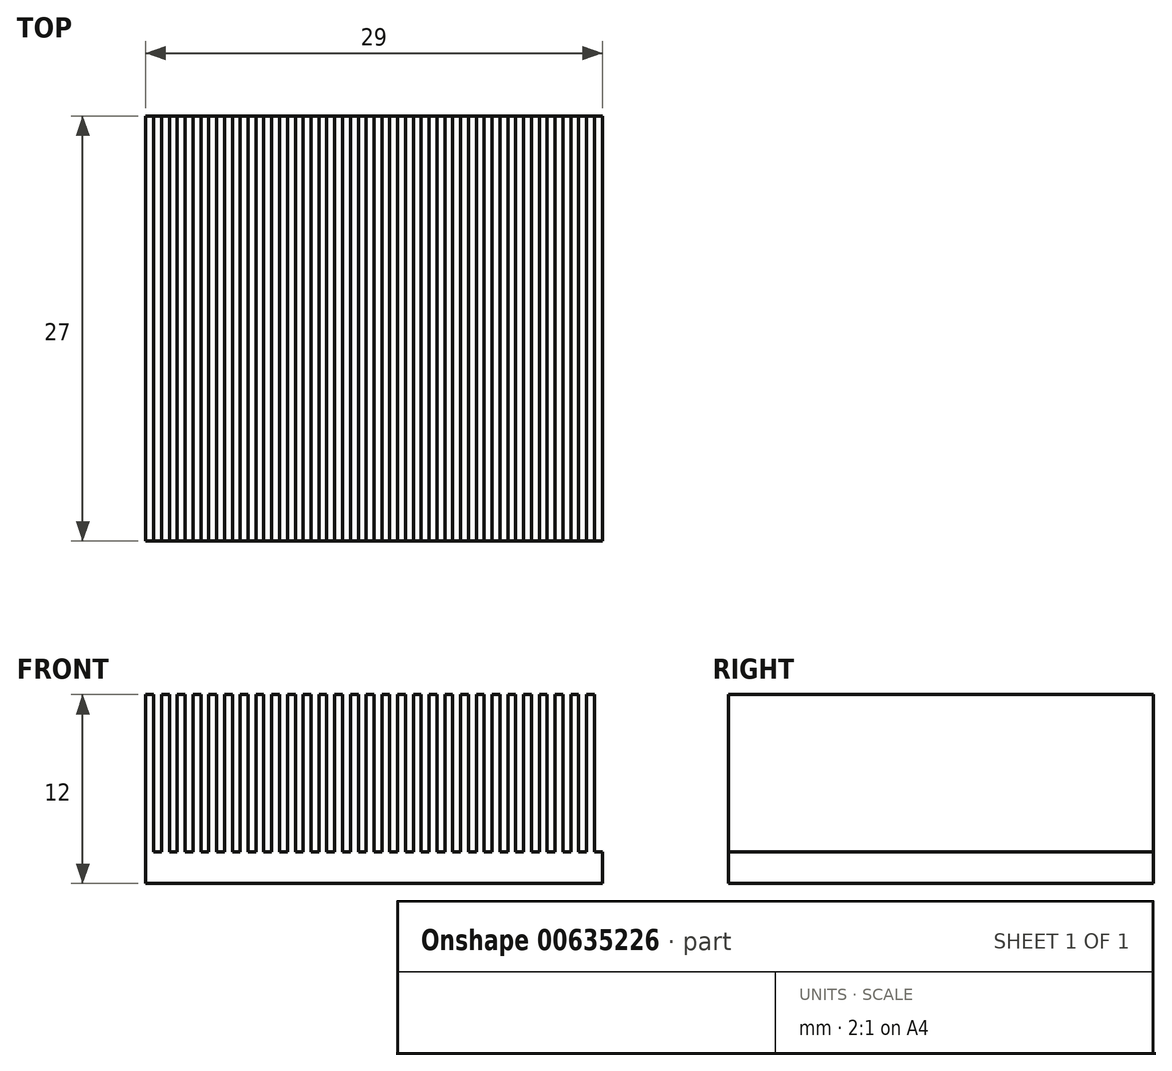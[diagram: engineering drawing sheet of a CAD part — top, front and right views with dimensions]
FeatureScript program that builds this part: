
annotation { "Feature Type Name" : "Feature", "Feature Type Description" : "" }
export const myFeature = defineFeature(function(context is Context, id is Id, definition is map)
    precondition{}
    {
        {
            var Q0;
            Q0=qCreatedBy(makeId("Top.planeOp"),FACE);
            var sketch = newSketch(context, id + "F0", { "sketchPlane" : qUnion([Q0])});
            skLineSegment(sketch, "E0.bottom", {"start": v(14.5, 13.5) * mm, "end": v(-14.5, 13.5) * mm});
            skLineSegment(sketch, "E0.top", {"start": v(14.5, -13.5) * mm, "end": v(-14.5, -13.5) * mm});
            skLineSegment(sketch, "E0.left", {"start": v(14.5, 13.5) * mm, "end": v(14.5, -13.5) * mm});
            skLineSegment(sketch, "E0.right", {"start": v(-14.5, 13.5) * mm, "end": v(-14.5, -13.5) * mm});
            skPoint(sketch, "E0.middle", {"position": v(0, 0) * mm});
            skSolve(sketch);
        }
        {
            var Q0;
            Q0 = qSketchRegion(id + "F0", true);
            extrude(context, id + "F1", {"entities" : qUnion([Q0]), "depth" : 2 * mm, "offsetDistance" : 25 * mm});
        }
        {
            var Q0;
            Q0=makeQuery(id+"F1.opExtrude","CAP_FACE",FACE,{"disambiguationData":[OSD([sQuery(id+"F0.wireOp",EDGE,"E0.bottom"),sQuery(id+"F0.wireOp",EDGE,"E0.top"),sQuery(id+"F0.wireOp",EDGE,"E0.left"),sQuery(id+"F0.wireOp",EDGE,"E0.right")])],"isStart":false});
            var sketch = newSketch(context, id + "F2", { "sketchPlane" : qUnion([Q0])});
            skLineSegment(sketch, "E1.bottom", {"start": v(-14.5, 13.5) * mm, "end": v(-14, 13.5) * mm});
            skLineSegment(sketch, "E1.top", {"start": v(-14.5, -13.5) * mm, "end": v(-14, -13.5) * mm});
            skLineSegment(sketch, "E1.left", {"start": v(-14.5, 13.5) * mm, "end": v(-14.5, -13.5) * mm});
            skLineSegment(sketch, "E1.right", {"start": v(-14, 13.5) * mm, "end": v(-14, -13.5) * mm});
            skLineSegment(sketch, "E2.1.0.0", {"start": v(-13.5, 13.5) * mm, "end": v(-13, 13.5) * mm});
            skLineSegment(sketch, "E2.1.0.1", {"start": v(-13.5, 13.5) * mm, "end": v(-13.5, -13.5) * mm});
            skLineSegment(sketch, "E2.1.0.2", {"start": v(-13, 13.5) * mm, "end": v(-13, -13.5) * mm});
            skLineSegment(sketch, "E2.1.0.3", {"start": v(-13.5, -13.5) * mm, "end": v(-13, -13.5) * mm});
            skLineSegment(sketch, "E2.2.0.0", {"start": v(-12.5, 13.5) * mm, "end": v(-12, 13.5) * mm});
            skLineSegment(sketch, "E2.2.0.1", {"start": v(-12.5, 13.5) * mm, "end": v(-12.5, -13.5) * mm});
            skLineSegment(sketch, "E2.2.0.2", {"start": v(-12, 13.5) * mm, "end": v(-12, -13.5) * mm});
            skLineSegment(sketch, "E2.2.0.3", {"start": v(-12.5, -13.5) * mm, "end": v(-12, -13.5) * mm});
            skLineSegment(sketch, "E2.3.0.0", {"start": v(-11.5, 13.5) * mm, "end": v(-11, 13.5) * mm});
            skLineSegment(sketch, "E2.3.0.1", {"start": v(-11.5, 13.5) * mm, "end": v(-11.5, -13.5) * mm});
            skLineSegment(sketch, "E2.3.0.2", {"start": v(-11, 13.5) * mm, "end": v(-11, -13.5) * mm});
            skLineSegment(sketch, "E2.3.0.3", {"start": v(-11.5, -13.5) * mm, "end": v(-11, -13.5) * mm});
            skLineSegment(sketch, "E2.4.0.0", {"start": v(-10.5, 13.5) * mm, "end": v(-10, 13.5) * mm});
            skLineSegment(sketch, "E2.4.0.1", {"start": v(-10.5, 13.5) * mm, "end": v(-10.5, -13.5) * mm});
            skLineSegment(sketch, "E2.4.0.2", {"start": v(-10, 13.5) * mm, "end": v(-10, -13.5) * mm});
            skLineSegment(sketch, "E2.4.0.3", {"start": v(-10.5, -13.5) * mm, "end": v(-10, -13.5) * mm});
            skLineSegment(sketch, "E2.5.0.0", {"start": v(-9.5, 13.5) * mm, "end": v(-9, 13.5) * mm});
            skLineSegment(sketch, "E2.5.0.1", {"start": v(-9.5, 13.5) * mm, "end": v(-9.5, -13.5) * mm});
            skLineSegment(sketch, "E2.5.0.2", {"start": v(-9, 13.5) * mm, "end": v(-9, -13.5) * mm});
            skLineSegment(sketch, "E2.5.0.3", {"start": v(-9.5, -13.5) * mm, "end": v(-9, -13.5) * mm});
            skLineSegment(sketch, "E2.6.0.0", {"start": v(-8.5, 13.5) * mm, "end": v(-8, 13.5) * mm});
            skLineSegment(sketch, "E2.6.0.1", {"start": v(-8.5, 13.5) * mm, "end": v(-8.5, -13.5) * mm});
            skLineSegment(sketch, "E2.6.0.2", {"start": v(-8, 13.5) * mm, "end": v(-8, -13.5) * mm});
            skLineSegment(sketch, "E2.6.0.3", {"start": v(-8.5, -13.5) * mm, "end": v(-8, -13.5) * mm});
            skLineSegment(sketch, "E2.7.0.0", {"start": v(-7.5, 13.5) * mm, "end": v(-7, 13.5) * mm});
            skLineSegment(sketch, "E2.7.0.1", {"start": v(-7.5, 13.5) * mm, "end": v(-7.5, -13.5) * mm});
            skLineSegment(sketch, "E2.7.0.2", {"start": v(-7, 13.5) * mm, "end": v(-7, -13.5) * mm});
            skLineSegment(sketch, "E2.7.0.3", {"start": v(-7.5, -13.5) * mm, "end": v(-7, -13.5) * mm});
            skLineSegment(sketch, "E2.8.0.0", {"start": v(-6.5, 13.5) * mm, "end": v(-6, 13.5) * mm});
            skLineSegment(sketch, "E2.8.0.1", {"start": v(-6.5, 13.5) * mm, "end": v(-6.5, -13.5) * mm});
            skLineSegment(sketch, "E2.8.0.2", {"start": v(-6, 13.5) * mm, "end": v(-6, -13.5) * mm});
            skLineSegment(sketch, "E2.8.0.3", {"start": v(-6.5, -13.5) * mm, "end": v(-6, -13.5) * mm});
            skLineSegment(sketch, "E2.9.0.0", {"start": v(-5.5, 13.5) * mm, "end": v(-5, 13.5) * mm});
            skLineSegment(sketch, "E2.9.0.1", {"start": v(-5.5, 13.5) * mm, "end": v(-5.5, -13.5) * mm});
            skLineSegment(sketch, "E2.9.0.2", {"start": v(-5, 13.5) * mm, "end": v(-5, -13.5) * mm});
            skLineSegment(sketch, "E2.9.0.3", {"start": v(-5.5, -13.5) * mm, "end": v(-5, -13.5) * mm});
            skLineSegment(sketch, "E2.10.0.0", {"start": v(-4.5, 13.5) * mm, "end": v(-4, 13.5) * mm});
            skLineSegment(sketch, "E2.10.0.1", {"start": v(-4.5, 13.5) * mm, "end": v(-4.5, -13.5) * mm});
            skLineSegment(sketch, "E2.10.0.2", {"start": v(-4, 13.5) * mm, "end": v(-4, -13.5) * mm});
            skLineSegment(sketch, "E2.10.0.3", {"start": v(-4.5, -13.5) * mm, "end": v(-4, -13.5) * mm});
            skLineSegment(sketch, "E2.11.0.0", {"start": v(-3.5, 13.5) * mm, "end": v(-3, 13.5) * mm});
            skLineSegment(sketch, "E2.11.0.1", {"start": v(-3.5, 13.5) * mm, "end": v(-3.5, -13.5) * mm});
            skLineSegment(sketch, "E2.11.0.2", {"start": v(-3, 13.5) * mm, "end": v(-3, -13.5) * mm});
            skLineSegment(sketch, "E2.11.0.3", {"start": v(-3.5, -13.5) * mm, "end": v(-3, -13.5) * mm});
            skLineSegment(sketch, "E2.12.0.0", {"start": v(-2.5, 13.5) * mm, "end": v(-2, 13.5) * mm});
            skLineSegment(sketch, "E2.12.0.1", {"start": v(-2.5, 13.5) * mm, "end": v(-2.5, -13.5) * mm});
            skLineSegment(sketch, "E2.12.0.2", {"start": v(-2, 13.5) * mm, "end": v(-2, -13.5) * mm});
            skLineSegment(sketch, "E2.12.0.3", {"start": v(-2.5, -13.5) * mm, "end": v(-2, -13.5) * mm});
            skLineSegment(sketch, "E2.13.0.0", {"start": v(-1.5, 13.5) * mm, "end": v(-1, 13.5) * mm});
            skLineSegment(sketch, "E2.13.0.1", {"start": v(-1.5, 13.5) * mm, "end": v(-1.5, -13.5) * mm});
            skLineSegment(sketch, "E2.13.0.2", {"start": v(-1, 13.5) * mm, "end": v(-1, -13.5) * mm});
            skLineSegment(sketch, "E2.13.0.3", {"start": v(-1.5, -13.5) * mm, "end": v(-1, -13.5) * mm});
            skLineSegment(sketch, "E2.14.0.0", {"start": v(-0.5, 13.5) * mm, "end": v(0, 13.5) * mm});
            skLineSegment(sketch, "E2.14.0.1", {"start": v(-0.5, 13.5) * mm, "end": v(-0.5, -13.5) * mm});
            skLineSegment(sketch, "E2.14.0.2", {"start": v(0, 13.5) * mm, "end": v(0, -13.5) * mm});
            skLineSegment(sketch, "E2.14.0.3", {"start": v(-0.5, -13.5) * mm, "end": v(0, -13.5) * mm});
            skLineSegment(sketch, "E2.15.0.0", {"start": v(0.5, 13.5) * mm, "end": v(1, 13.5) * mm});
            skLineSegment(sketch, "E2.15.0.1", {"start": v(0.5, 13.5) * mm, "end": v(0.5, -13.5) * mm});
            skLineSegment(sketch, "E2.15.0.2", {"start": v(1, 13.5) * mm, "end": v(1, -13.5) * mm});
            skLineSegment(sketch, "E2.15.0.3", {"start": v(0.5, -13.5) * mm, "end": v(1, -13.5) * mm});
            skLineSegment(sketch, "E2.16.0.0", {"start": v(1.5, 13.5) * mm, "end": v(2, 13.5) * mm});
            skLineSegment(sketch, "E2.16.0.1", {"start": v(1.5, 13.5) * mm, "end": v(1.5, -13.5) * mm});
            skLineSegment(sketch, "E2.16.0.2", {"start": v(2, 13.5) * mm, "end": v(2, -13.5) * mm});
            skLineSegment(sketch, "E2.16.0.3", {"start": v(1.5, -13.5) * mm, "end": v(2, -13.5) * mm});
            skLineSegment(sketch, "E2.17.0.0", {"start": v(2.5, 13.5) * mm, "end": v(3, 13.5) * mm});
            skLineSegment(sketch, "E2.17.0.1", {"start": v(2.5, 13.5) * mm, "end": v(2.5, -13.5) * mm});
            skLineSegment(sketch, "E2.17.0.2", {"start": v(3, 13.5) * mm, "end": v(3, -13.5) * mm});
            skLineSegment(sketch, "E2.17.0.3", {"start": v(2.5, -13.5) * mm, "end": v(3, -13.5) * mm});
            skLineSegment(sketch, "E2.18.0.0", {"start": v(3.5, 13.5) * mm, "end": v(4, 13.5) * mm});
            skLineSegment(sketch, "E2.18.0.1", {"start": v(3.5, 13.5) * mm, "end": v(3.5, -13.5) * mm});
            skLineSegment(sketch, "E2.18.0.2", {"start": v(4, 13.5) * mm, "end": v(4, -13.5) * mm});
            skLineSegment(sketch, "E2.18.0.3", {"start": v(3.5, -13.5) * mm, "end": v(4, -13.5) * mm});
            skLineSegment(sketch, "E2.direction1", {"start": v(-14.5, 13.5) * mm, "end": v(-13.5, 13.5) * mm, "construction": true});
            skLineSegment(sketch, "E3.0.19.0", {"start": v(4.5, 13.5) * mm, "end": v(5, 13.5) * mm});
            skLineSegment(sketch, "E3.3.19.0", {"start": v(4.5, 13.5) * mm, "end": v(4.5, -13.5) * mm});
            skLineSegment(sketch, "E3.6.19.0", {"start": v(5, 13.5) * mm, "end": v(5, -13.5) * mm});
            skLineSegment(sketch, "E3.9.19.0", {"start": v(4.5, -13.5) * mm, "end": v(5, -13.5) * mm});
            skLineSegment(sketch, "E4.0.20.0", {"start": v(5.5, 13.5) * mm, "end": v(6, 13.5) * mm});
            skLineSegment(sketch, "E4.3.20.0", {"start": v(5.5, 13.5) * mm, "end": v(5.5, -13.5) * mm});
            skLineSegment(sketch, "E4.6.20.0", {"start": v(6, 13.5) * mm, "end": v(6, -13.5) * mm});
            skLineSegment(sketch, "E4.9.20.0", {"start": v(5.5, -13.5) * mm, "end": v(6, -13.5) * mm});
            skLineSegment(sketch, "E5.0.21.0", {"start": v(6.5, 13.5) * mm, "end": v(7, 13.5) * mm});
            skLineSegment(sketch, "E5.3.21.0", {"start": v(6.5, 13.5) * mm, "end": v(6.5, -13.5) * mm});
            skLineSegment(sketch, "E5.6.21.0", {"start": v(7, 13.5) * mm, "end": v(7, -13.5) * mm});
            skLineSegment(sketch, "E5.9.21.0", {"start": v(6.5, -13.5) * mm, "end": v(7, -13.5) * mm});
            skLineSegment(sketch, "E6.0.22.0", {"start": v(7.5, 13.5) * mm, "end": v(8, 13.5) * mm});
            skLineSegment(sketch, "E6.3.22.0", {"start": v(7.5, 13.5) * mm, "end": v(7.5, -13.5) * mm});
            skLineSegment(sketch, "E6.6.22.0", {"start": v(8, 13.5) * mm, "end": v(8, -13.5) * mm});
            skLineSegment(sketch, "E6.9.22.0", {"start": v(7.5, -13.5) * mm, "end": v(8, -13.5) * mm});
            skLineSegment(sketch, "E7.0.23.0", {"start": v(8.5, 13.5) * mm, "end": v(9, 13.5) * mm});
            skLineSegment(sketch, "E7.3.23.0", {"start": v(8.5, 13.5) * mm, "end": v(8.5, -13.5) * mm});
            skLineSegment(sketch, "E7.6.23.0", {"start": v(9, 13.5) * mm, "end": v(9, -13.5) * mm});
            skLineSegment(sketch, "E7.9.23.0", {"start": v(8.5, -13.5) * mm, "end": v(9, -13.5) * mm});
            skLineSegment(sketch, "E8.0.24.0", {"start": v(9.5, 13.5) * mm, "end": v(10, 13.5) * mm});
            skLineSegment(sketch, "E8.3.24.0", {"start": v(9.5, 13.5) * mm, "end": v(9.5, -13.5) * mm});
            skLineSegment(sketch, "E8.6.24.0", {"start": v(10, 13.5) * mm, "end": v(10, -13.5) * mm});
            skLineSegment(sketch, "E8.9.24.0", {"start": v(9.5, -13.5) * mm, "end": v(10, -13.5) * mm});
            skLineSegment(sketch, "E9.0.25.0", {"start": v(10.5, 13.5) * mm, "end": v(11, 13.5) * mm});
            skLineSegment(sketch, "E9.3.25.0", {"start": v(10.5, 13.5) * mm, "end": v(10.5, -13.5) * mm});
            skLineSegment(sketch, "E9.6.25.0", {"start": v(11, 13.5) * mm, "end": v(11, -13.5) * mm});
            skLineSegment(sketch, "E9.9.25.0", {"start": v(10.5, -13.5) * mm, "end": v(11, -13.5) * mm});
            skLineSegment(sketch, "E10.0.26.0", {"start": v(11.5, 13.5) * mm, "end": v(12, 13.5) * mm});
            skLineSegment(sketch, "E10.3.26.0", {"start": v(11.5, 13.5) * mm, "end": v(11.5, -13.5) * mm});
            skLineSegment(sketch, "E10.6.26.0", {"start": v(12, 13.5) * mm, "end": v(12, -13.5) * mm});
            skLineSegment(sketch, "E10.9.26.0", {"start": v(11.5, -13.5) * mm, "end": v(12, -13.5) * mm});
            skLineSegment(sketch, "E11.0.27.0", {"start": v(12.5, 13.5) * mm, "end": v(13, 13.5) * mm});
            skLineSegment(sketch, "E11.3.27.0", {"start": v(12.5, 13.5) * mm, "end": v(12.5, -13.5) * mm});
            skLineSegment(sketch, "E11.6.27.0", {"start": v(13, 13.5) * mm, "end": v(13, -13.5) * mm});
            skLineSegment(sketch, "E11.9.27.0", {"start": v(12.5, -13.5) * mm, "end": v(13, -13.5) * mm});
            skLineSegment(sketch, "E11.0.28.0", {"start": v(13.5, 13.5) * mm, "end": v(14, 13.5) * mm});
            skLineSegment(sketch, "E11.3.28.0", {"start": v(13.5, 13.5) * mm, "end": v(13.5, -13.5) * mm});
            skLineSegment(sketch, "E11.6.28.0", {"start": v(14, 13.5) * mm, "end": v(14, -13.5) * mm});
            skLineSegment(sketch, "E11.9.28.0", {"start": v(13.5, -13.5) * mm, "end": v(14, -13.5) * mm});
            skSolve(sketch);
        }
        {
            var Q0;
            Q0 = qSketchRegion(id + "F2", true);
            extrude(context, id + "F3", {"entities" : qUnion([Q0]), "operationType" : NewBodyOperationType.ADD, "depth" : 10 * mm, "offsetDistance" : 25 * mm});
        }
    });
